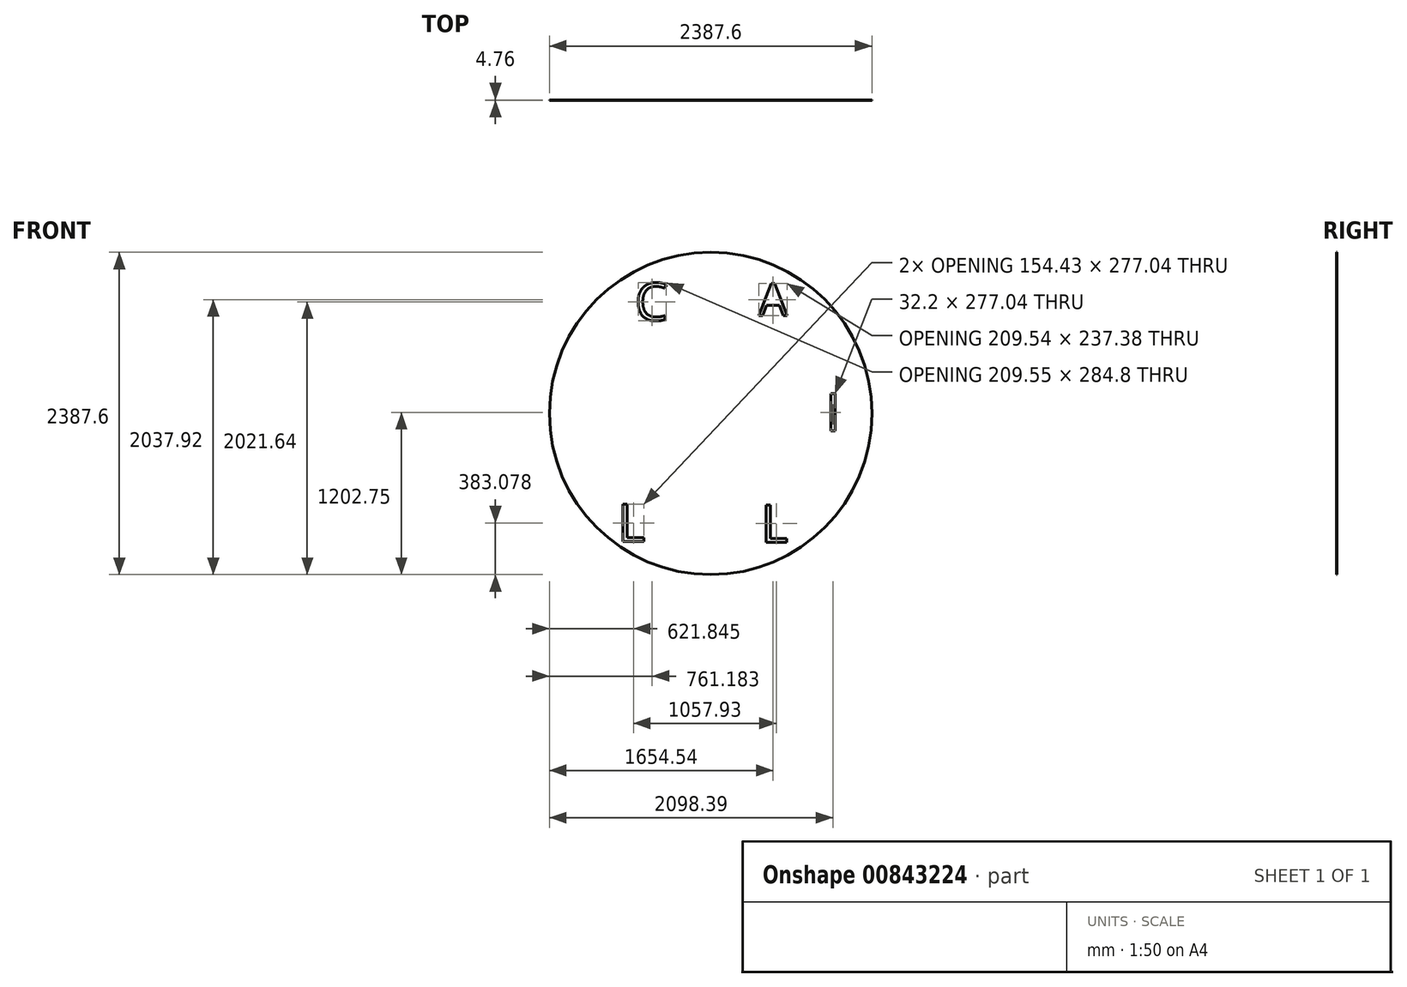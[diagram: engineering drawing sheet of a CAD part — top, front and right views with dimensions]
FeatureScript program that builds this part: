
annotation { "Feature Type Name" : "Feature", "Feature Type Description" : "" }
export const myFeature = defineFeature(function(context is Context, id is Id, definition is map)
    precondition{}
    {
        {
            var Q0;
            Q0=qCreatedBy(makeId("Front.planeOp"),FACE);
            var sketch = newSketch(context, id + "F0", { "sketchPlane" : qUnion([Q0])});
            skCircle(sketch, "E0", {"center": v(1098.53, 1422.67) * mm, "radius": 1193.8 * mm});
            skText(sketch, "E1", { "text": "C\n", "fontName": "OpenSans-Regular.ttf"});
            skText(sketch, "E2", { "text": "A\n", "fontName": "OpenSans-Regular.ttf"});
            skCircle(sketch, "E3", {"center": v(307.6, 1954.1) * mm, "radius": 240.92 * mm});
            skCircle(sketch, "E4", {"center": v(1116.01, 2375.4) * mm, "radius": 240.92 * mm});
            skCircle(sketch, "E5", {"center": v(1926.44, 1894.42) * mm, "radius": 240.92 * mm});
            skText(sketch, "E6", { "text": "H\n", "fontName": "OpenSans-Regular.ttf"});
            skText(sketch, "E7", { "text": "I\n", "fontName": "OpenSans-Regular.ttf"});
            skCircle(sketch, "E8", {"center": v(214.25, 1067.66) * mm, "radius": 240.92 * mm});
            skCircle(sketch, "E9", {"center": v(1944.87, 984.85) * mm, "radius": 240.92 * mm});
            skCircle(sketch, "E10", {"center": v(1080.22, 469.97) * mm, "radius": 240.92 * mm});
            skText(sketch, "E11", { "text": "L\n", "fontName": "OpenSans-Regular.ttf"});
            skText(sketch, "E12", { "text": "L\n", "fontName": "OpenSans-Regular.ttf"});
            skLineSegment(sketch, "E13", {"start": v(978.64, 1338.67) * mm, "end": v(1098.53, 1562.6) * mm});
            skLineSegment(sketch, "E14", {"start": v(1098.53, 1562.6) * mm, "end": v(1232.51, 1346.81) * mm});
            skLineSegment(sketch, "E15", {"start": v(1232.51, 1346.81) * mm, "end": v(978.64, 1338.67) * mm});
            skCircle(sketch, "E16", {"center": v(1098.53, 1422.67) * mm, "radius": 52.45 * mm});
            const initialGuessF0  = {"E1": [0.53743, 2.11193, 1, 0, 0.2794], "E2": [1.4545, 2.1481, 1, 0, 0.23841], "E6": [0, 1.37775, 1, 0, 0.2794], "E7": [1.94894, 1.2931, 1, 0, 0.2794], "E11": [0.41128, 0.47343, 1, 0, 0.2794], "E12": [1.46921, 0.4678, 1, 0, 0.2794]};
            skSetInitialGuess(sketch, initialGuessF0);
            skSolve(sketch);
        }
        {
            var Q0;
            Q0=makeQuery(id+"F0.imprint","IMPRINT",FACE,{"disambiguationData":[TD([[makeQuery(id+"F0.imprint","IMPRINT",EDGE,{"derivedFrom":sQuery(id+"F0.wireOp",EDGE,"E1.sketch_text.stroke-0")}),1.0]])]});
            var Q1;
            Q1=makeQuery(id+"F0.imprint","IMPRINT",FACE,{"disambiguationData":[TD([[makeQuery(id+"F0.imprint","IMPRINT",EDGE,{"derivedFrom":sQuery(id+"F0.wireOp",EDGE,"E3")}),1.0]])]});
            var Q2;
            Q2=makeQuery(id+"F0.imprint","IMPRINT",FACE,{"disambiguationData":[TD([[makeQuery(id+"F0.imprint","IMPRINT",EDGE,{"derivedFrom":sQuery(id+"F0.wireOp",EDGE,"E8")}),1.0]])]});
            var Q3;
            Q3=makeQuery(id+"F0.imprint","IMPRINT",FACE,{"disambiguationData":[TD([[makeQuery(id+"F0.imprint","IMPRINT",EDGE,{"derivedFrom":sQuery(id+"F0.wireOp",EDGE,"E10")}),1.0]])]});
            var Q4;
            Q4=makeQuery(id+"F0.imprint","IMPRINT",FACE,{"disambiguationData":[TD([[makeQuery(id+"F0.imprint","IMPRINT",EDGE,{"derivedFrom":sQuery(id+"F0.wireOp",EDGE,"E13")}),-1.0]])]});
            var Q5;
            Q5=makeQuery(id+"F0.imprint","IMPRINT",FACE,{"disambiguationData":[TD([[makeQuery(id+"F0.imprint","IMPRINT",EDGE,{"derivedFrom":sQuery(id+"F0.wireOp",EDGE,"E4")}),1.0]])]});
            var Q6;
            Q6=makeQuery(id+"F0.imprint","IMPRINT",FACE,{"disambiguationData":[TD([[makeQuery(id+"F0.imprint","IMPRINT",EDGE,{"derivedFrom":sQuery(id+"F0.wireOp",EDGE,"E16")}),1.0]])]});
            var Q7;
            Q7 = qSketchRegion(id + "F0", true);
            var Q8;
            Q8=makeQuery(id+"F0.imprint","IMPRINT",FACE,{"disambiguationData":[TD([[makeQuery(id+"F0.imprint","IMPRINT",EDGE,{"derivedFrom":sQuery(id+"F0.wireOp",EDGE,"E6.sketch_text.stroke-0")}),-1.0]])]});
            extrude(context, id + "F1", {"entities" : qUnion([Q0, Q1, Q2, Q3, Q4, Q5, Q6, Q7, Q8]), "depth" : 4.76 * mm, "offsetDistance" : 25 * mm});
        }
    });
